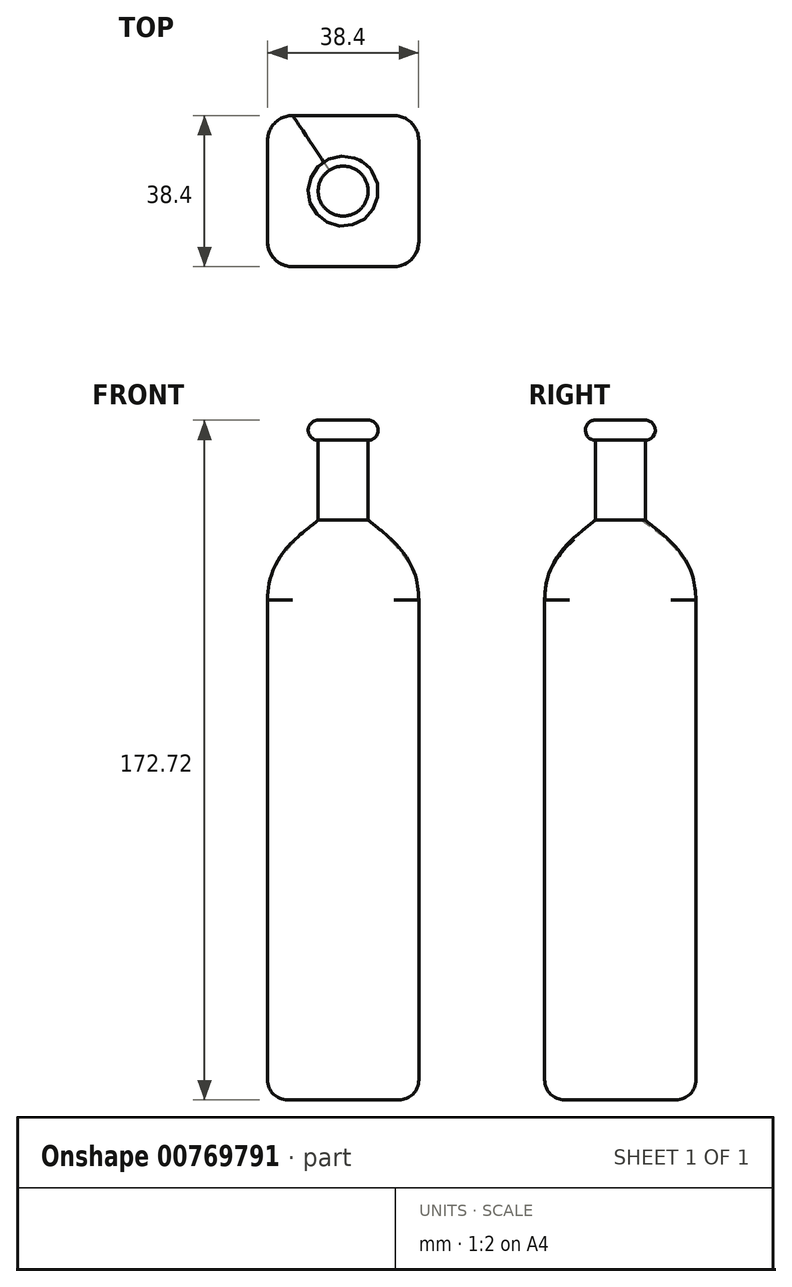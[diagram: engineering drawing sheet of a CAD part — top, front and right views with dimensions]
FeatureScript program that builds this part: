
annotation { "Feature Type Name" : "Feature", "Feature Type Description" : "" }
export const myFeature = defineFeature(function(context is Context, id is Id, definition is map)
    precondition{}
    {
        {
            var Q0;
            Q0=qCreatedBy(makeId("Front.planeOp"),FACE);
            var sketch = newSketch(context, id + "F0", { "sketchPlane" : qUnion([Q0])});
            skLineSegment(sketch, "E0", {"start": v(0, 0) * mm, "end": v(0, 177.8) * mm, "construction": true});
            skPoint(sketch, "E1", {"position": v(0, 147.32) * mm});
            skPoint(sketch, "E2", {"position": v(0, 127) * mm});
            skSolve(sketch);
        }
        {
            var Q0;
            Q0=qCreatedBy(makeId("Top.planeOp"),FACE);
            var sketch = newSketch(context, id + "F1", { "sketchPlane" : qUnion([Q0])});
            skLineSegment(sketch, "E3.bottom", {"start": v(-12.85, 19.2) * mm, "end": v(12.85, 19.2) * mm});
            skLineSegment(sketch, "E3.top", {"start": v(-12.85, -19.2) * mm, "end": v(12.85, -19.2) * mm});
            skLineSegment(sketch, "E3.left", {"start": v(-19.2, 12.85) * mm, "end": v(-19.2, -12.85) * mm});
            skLineSegment(sketch, "E3.right", {"start": v(19.2, 12.85) * mm, "end": v(19.2, -12.85) * mm});
            skPoint(sketch, "E3.middle", {"position": v(0, 0) * mm});
            skPoint(sketch, "E4.visualSharp", {"position": v(-19.2, -19.2) * mm});
            skArc(sketch, "E4.filletArc", {"start": v(-19.2, -12.85) * mm, "mid": v(-17.34, -17.34) * mm, "end": v(-12.85, -19.2) * mm});
            skPoint(sketch, "E5.visualSharp", {"position": v(-19.2, 19.2) * mm});
            skArc(sketch, "E5.filletArc", {"start": v(-12.85, 19.2) * mm, "mid": v(-17.34, 17.34) * mm, "end": v(-19.2, 12.85) * mm});
            skPoint(sketch, "E6.visualSharp", {"position": v(19.2, 19.2) * mm});
            skArc(sketch, "E6.filletArc", {"start": v(19.2, 12.85) * mm, "mid": v(17.34, 17.34) * mm, "end": v(12.85, 19.2) * mm});
            skPoint(sketch, "E7.visualSharp", {"position": v(19.2, -19.2) * mm});
            skArc(sketch, "E7.filletArc", {"start": v(12.85, -19.2) * mm, "mid": v(17.34, -17.34) * mm, "end": v(19.2, -12.85) * mm});
            skSolve(sketch);
        }
        {
            var Q0;
            Q0=makeQuery(id+"F1.imprint","IMPRINT",FACE,{"disambiguationData":[TD([[makeQuery(id+"F1.imprint","IMPRINT",EDGE,{"derivedFrom":sQuery(id+"F1.wireOp",EDGE,"E3.bottom")}),-1.0]])]});
            extrude(context, id + "F2", {"entities" : qUnion([Q0]), "depth" : 127 * mm, "offsetDistance" : 25.4 * mm});
        }
        {
            var Q0;
            Q0=makeQuery(id+"F2.opExtrude","CAP_EDGE",EDGE,{"disambiguationData":[OSD([sQuery(id+"F1.wireOp",EDGE,"E3.top")])],"isStart":true});
            fillet(context, id + "F3", {"entities" : qUnion([Q0]), "radius" : 5.08 * mm, "tangentPropagation" : true, "allowEdgeOverflow" : false});
        }
        {
            var Q0;
            Q0=makeQuery(id+"F2.opExtrude","SWEPT_FACE",FACE,{"disambiguationData":[OSD([sQuery(id+"F1.wireOp",EDGE,"E4.filletArc")])]});
            var Q1;
            Q1=sQuery(id+"F0.wireOp",VERTEX,"E1");
            cPlane(context, id + "F4", {"entities" : qUnion([Q0, Q1]), "cplaneType" : CPlaneType.LINE_POINT, "offset" : 25.4 * mm, "width" : 152.4 * mm, "height" : 152.4 * mm});
        }
        {
            var Q0;
            Q0=qCreatedBy(id+"F4.planeOp",FACE);
            var sketch = newSketch(context, id + "F5", { "sketchPlane" : qUnion([Q0])});
            skCircle(sketch, "E8", {"center": v(0, 0) * mm, "radius": 6.35 * mm});
            skSolve(sketch);
        }
        {
            var Q1;
            Q1=makeQuery(id+"F2.opExtrude","CAP_FACE",FACE,{"disambiguationData":[OSD([sQuery(id+"F1.wireOp",EDGE,"E3.bottom"),sQuery(id+"F1.wireOp",EDGE,"E3.top"),sQuery(id+"F1.wireOp",EDGE,"E3.left"),sQuery(id+"F1.wireOp",EDGE,"E3.right"),sQuery(id+"F1.wireOp",EDGE,"E4.filletArc"),sQuery(id+"F1.wireOp",EDGE,"E5.filletArc"),sQuery(id+"F1.wireOp",EDGE,"E6.filletArc"),sQuery(id+"F1.wireOp",EDGE,"E7.filletArc")])],"isStart":false});
            var Q2;
            Q2=makeQuery(id+"F5.imprint","IMPRINT",FACE,{"disambiguationData":[TD([[makeQuery(id+"F5.imprint","IMPRINT",EDGE,{"derivedFrom":sQuery(id+"F5.wireOp",EDGE,"E8")}),1.0]])]});
            var Q3;
            Q3=sQuery(id+"FJX253icgoC206J_1.wireOp",EDGE,"3dc4171a-6a4f-4890-810d-a7d4722ee7d10.MirrorCS");
            var Q4;
            Q4=sQuery(id+"FJX253icgoC206J_1.wireOp",EDGE,"xryahjjU-2WOz-Yf1O-6DoU-3T0hrYgmwLhE");
            loft(context, id + "F6", {"operationType" : NewBodyOperationType.ADD, "startCondition" : LoftEndDerivativeType.MATCH_TANGENT, "startMagnitude" : 1.5, "sheetProfilesArray" : [{ "sheetProfileEntities" : qUnion([Q1]) }, { "sheetProfileEntities" : qUnion([Q2]) }], "guidesArray" : [{ "guideEntities" : qUnion([Q3]), "guideDerivativeType" : LoftGuideDerivativeType.DEFAULT, "guideDerivativeMagnitude" : 1 }, { "guideEntities" : qUnion([Q4]), "guideDerivativeType" : LoftGuideDerivativeType.DEFAULT, "guideDerivativeMagnitude" : 1 }]});
        }
        {
            var Q0;
            Q0=makeQuery(id+"F6.opLoft","CAP_FACE",FACE,{"disambiguationData":[OSD([makeQuery(id+"F5.imprint","IMPRINT",FACE,{"disambiguationData":[TD([[makeQuery(id+"F5.imprint","IMPRINT",EDGE,{"derivedFrom":sQuery(id+"F5.wireOp",EDGE,"E8")}),1.0]])]})])],"isStart":true});
            extrude(context, id + "F7", {"entities" : qUnion([Q0]), "operationType" : NewBodyOperationType.ADD, "depth" : 25.4 * mm, "offsetDistance" : 25.4 * mm});
        }
        {
            var Q0;
            Q0=makeQuery(id+"F7.opExtrude","CAP_FACE",FACE,{"disambiguationData":[OSD([makeQuery(id+"F5.imprint","IMPRINT",FACE,{"disambiguationData":[TD([[makeQuery(id+"F5.imprint","IMPRINT",EDGE,{"derivedFrom":sQuery(id+"F5.wireOp",EDGE,"E8")}),1.0]])]})])],"isStart":false});
            var sketch = newSketch(context, id + "F8", { "sketchPlane" : qUnion([Q0])});
            skLineSegment(sketch, "E9", {"start": v(-1.23, 6.23) * mm, "end": v(4.68, 7.4) * mm, "construction": true});
            skSolve(sketch);
        }
        {
            var Q0;
            Q0=sQuery(id+"F8.wireOp",EDGE,"E9");
            var Q1;
            Q1=sQuery(id+"F8.wireOp",VERTEX,"E9.start");
            cPlane(context, id + "F9", {"entities" : qUnion([Q0, Q1]), "cplaneType" : CPlaneType.LINE_POINT, "offset" : 25.4 * mm, "width" : 152.4 * mm, "height" : 152.4 * mm});
        }
        {
            var Q0;
            Q0=qCreatedBy(id+"F9.planeOp",FACE);
            var sketch = newSketch(context, id + "F10", { "sketchPlane" : qUnion([Q0])});
            skPoint(sketch, "E10.0", {"position": v(6.35, 172.72) * mm});
            skLineSegment(sketch, "E11", {"start": v(6.35, 172.72) * mm, "end": v(6.35, 147.32) * mm});
            skLineSegment(sketch, "E12", {"start": v(6.35, 172.72) * mm, "end": v(0, 172.72) * mm, "construction": true});
            skArc(sketch, "E13", {"start": v(6.35, 167.64) * mm, "mid": v(8.9, 170.18) * mm, "end": v(6.35, 172.72) * mm});
            skSolve(sketch);
        }
        {
            var Q0;
            {var subQ0=sQuery(id+"F10.wireOp",EDGE,"E13");Q0=makeQuery(id+"F10.imprint","IMPRINT",FACE,{"disambiguationData":[TD([[makeQuery(id+"F10.imprint","IMPRINT",EDGE,{"derivedFrom":subQ0}),1.0]])]});}
            var Q1;
            Q1=sQuery(id+"F0.wireOp",EDGE,"E0");
            revolve(context, id + "F11", {"operationType" : NewBodyOperationType.ADD, "surfaceOperationType" : NewSurfaceOperationType.NEW, "entities" : qUnion([Q0]), "axis" : qUnion([Q1]), "revolveType" : RevolveType.FULL});
        }
    });
